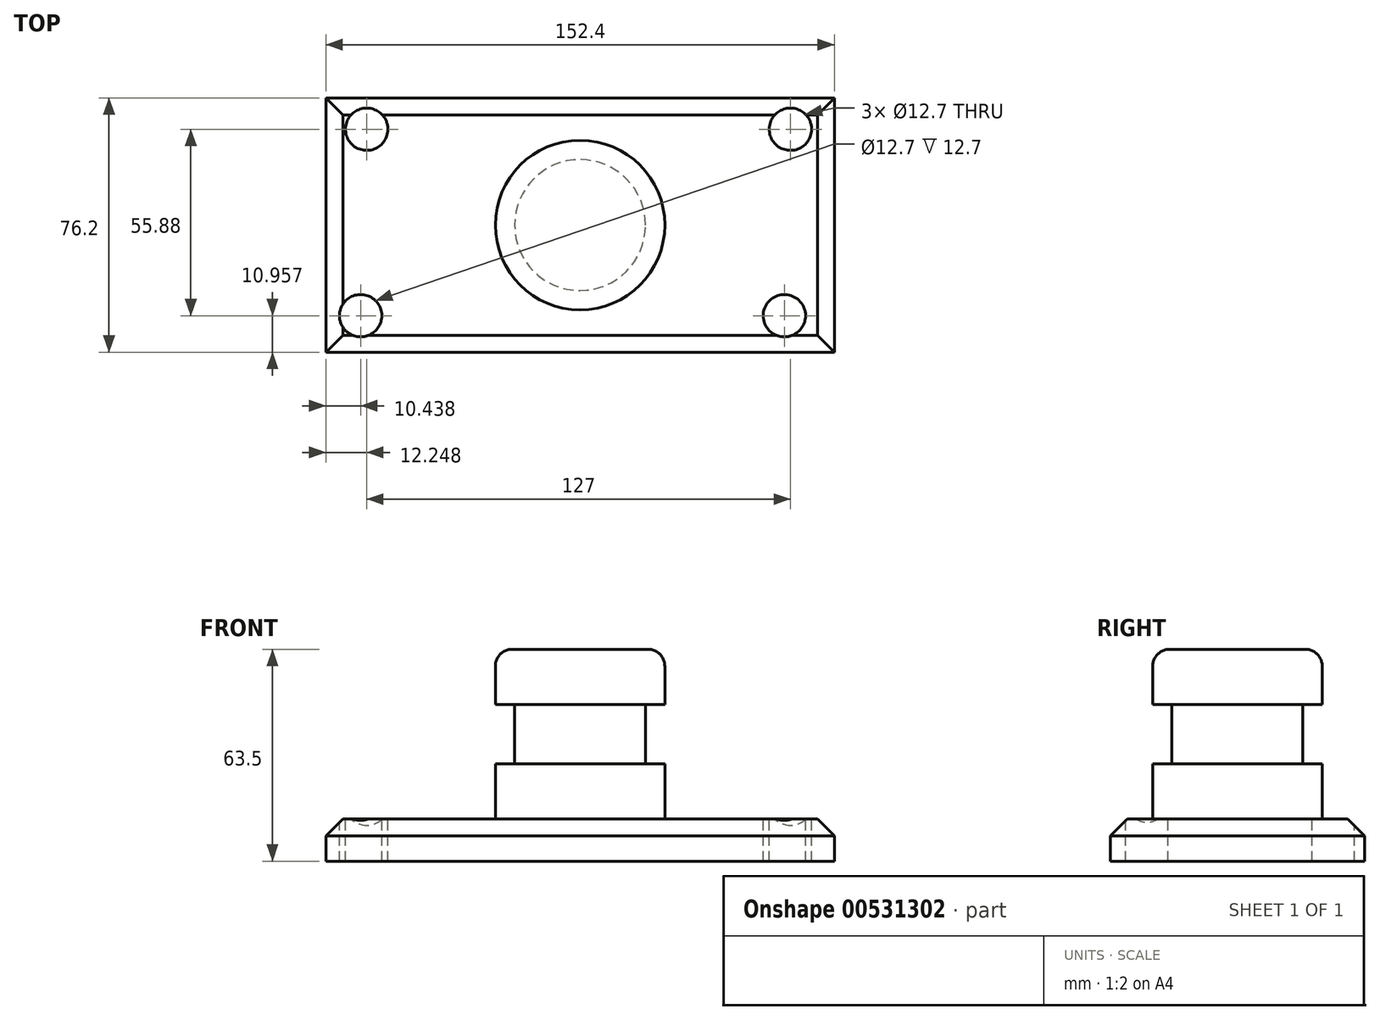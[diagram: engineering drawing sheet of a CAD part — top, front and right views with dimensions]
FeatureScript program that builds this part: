
annotation { "Feature Type Name" : "Feature", "Feature Type Description" : "" }
export const myFeature = defineFeature(function(context is Context, id is Id, definition is map)
    precondition{}
    {
        {
            var Q0;
            Q0=qCreatedBy(makeId("Top.planeOp"),FACE);
            var sketch = newSketch(context, id + "F0", { "sketchPlane" : qUnion([Q0])});
            skLineSegment(sketch, "E0.bottom", {"start": v(76.2, -38.1) * mm, "end": v(-76.2, -38.1) * mm});
            skLineSegment(sketch, "E0.top", {"start": v(76.2, 38.1) * mm, "end": v(-76.2, 38.1) * mm});
            skLineSegment(sketch, "E0.left", {"start": v(76.2, -38.1) * mm, "end": v(76.2, 38.1) * mm});
            skLineSegment(sketch, "E0.right", {"start": v(-76.2, -38.1) * mm, "end": v(-76.2, 38.1) * mm});
            skPoint(sketch, "E0.middle", {"position": v(0, 0) * mm});
            skSolve(sketch);
        }
        {
            var Q0;
            Q0 = qSketchRegion(id + "F0", true);
            extrude(context, id + "F1", {"entities" : qUnion([Q0]), "depth" : 12.7 * mm, "offsetDistance" : 25.4 * mm});
        }
        {
            var Q0;
            Q0=makeQuery(id+"F1.opExtrude","CAP_FACE",FACE,{"disambiguationData":[OSD([sQuery(id+"F0.wireOp",EDGE,"E0.bottom"),sQuery(id+"F0.wireOp",EDGE,"E0.top"),sQuery(id+"F0.wireOp",EDGE,"E0.left"),sQuery(id+"F0.wireOp",EDGE,"E0.right")])],"isStart":false});
            var sketch = newSketch(context, id + "F2", { "sketchPlane" : qUnion([Q0])});
            skCircle(sketch, "E1", {"center": v(-63.95, 28.74) * mm, "radius": 6.35 * mm});
            skCircle(sketch, "E2", {"center": v(-65.76, -27.14) * mm, "radius": 6.35 * mm});
            skCircle(sketch, "E3", {"center": v(61.24, -27.14) * mm, "radius": 6.35 * mm});
            skCircle(sketch, "E4", {"center": v(63.05, 28.74) * mm, "radius": 6.35 * mm});
            skSolve(sketch);
        }
        {
            var Q0;
            Q0=makeQuery(id+"F2.imprint","IMPRINT",FACE,{"disambiguationData":[TD([[makeQuery(id+"F2.imprint","IMPRINT",EDGE,{"derivedFrom":sQuery(id+"F2.wireOp",EDGE,"E1")}),1.0]])]});
            var Q1;
            Q1=makeQuery(id+"F2.imprint","IMPRINT",FACE,{"disambiguationData":[TD([[makeQuery(id+"F2.imprint","IMPRINT",EDGE,{"derivedFrom":sQuery(id+"F2.wireOp",EDGE,"E2")}),1.0]])]});
            var Q2;
            Q2=makeQuery(id+"F2.imprint","IMPRINT",FACE,{"disambiguationData":[TD([[makeQuery(id+"F2.imprint","IMPRINT",EDGE,{"derivedFrom":sQuery(id+"F2.wireOp",EDGE,"E4")}),1.0]])]});
            var Q3;
            Q3=makeQuery(id+"F2.imprint","IMPRINT",FACE,{"disambiguationData":[TD([[makeQuery(id+"F2.imprint","IMPRINT",EDGE,{"derivedFrom":sQuery(id+"F2.wireOp",EDGE,"E3")}),1.0]])]});
            extrude(context, id + "F3", {"entities" : qUnion([Q0, Q1, Q2, Q3]), "operationType" : NewBodyOperationType.REMOVE, "endBound" : BoundingType.THROUGH_ALL, "oppositeDirection" : true, "depth" : 12.7 * mm, "offsetDistance" : 25.4 * mm});
        }
        {
            var Q0;
            Q0=qCreatedBy(makeId("Front.planeOp"),FACE);
            var sketch = newSketch(context, id + "F4", { "sketchPlane" : qUnion([Q0])});
            skLineSegment(sketch, "E5.bottom", {"start": v(0, 12.7) * mm, "end": v(25.4, 12.7) * mm});
            skLineSegment(sketch, "E5.top", {"start": v(0, 63.5) * mm, "end": v(25.4, 63.5) * mm});
            skLineSegment(sketch, "E5.left", {"start": v(0, 12.7) * mm, "end": v(0, 63.5) * mm});
            skLineSegment(sketch, "E5.right", {"start": v(25.4, 12.7) * mm, "end": v(25.4, 63.5) * mm});
            skSolve(sketch);
        }
        {
            var Q0;
            Q0=makeQuery(id+"F4.imprint","IMPRINT",FACE,{"disambiguationData":[TD([[makeQuery(id+"F4.imprint","IMPRINT",EDGE,{"derivedFrom":sQuery(id+"F4.wireOp",EDGE,"E5.bottom")}),1.0]])]});
            var Q1;
            Q1=sQuery(id+"F4.wireOp",EDGE,"E5.left");
            revolve(context, id + "F5", {"operationType" : NewBodyOperationType.ADD, "entities" : qUnion([Q0]), "axis" : qUnion([Q1]), "revolveType" : RevolveType.FULL});
        }
        {
            var Q0;
            Q0=qCreatedBy(makeId("Front.planeOp"),FACE);
            var sketch = newSketch(context, id + "F6", { "sketchPlane" : qUnion([Q0])});
            skLineSegment(sketch, "E6.bottom", {"start": v(19.62, 46.99) * mm, "end": v(30.98, 46.99) * mm});
            skLineSegment(sketch, "E6.top", {"start": v(19.62, 29.2) * mm, "end": v(30.98, 29.2) * mm});
            skLineSegment(sketch, "E6.left", {"start": v(19.62, 46.99) * mm, "end": v(19.62, 29.2) * mm});
            skLineSegment(sketch, "E6.right", {"start": v(30.98, 46.99) * mm, "end": v(30.98, 29.2) * mm});
            skSolve(sketch);
        }
        {
            var Q0;
            Q0=makeQuery(id+"F6.imprint","IMPRINT",FACE,{"disambiguationData":[TD([[makeQuery(id+"F6.imprint","IMPRINT",EDGE,{"derivedFrom":sQuery(id+"F6.wireOp",EDGE,"E6.bottom")}),-1.0]])]});
            var Q1;
            Q1=makeQuery(id+"F5.opRevolve","SWEPT_FACE",FACE,{"disambiguationData":[OSD([sQuery(id+"F4.wireOp",EDGE,"E5.right")])]});
            revolve(context, id + "F7", {"operationType" : NewBodyOperationType.REMOVE, "entities" : qUnion([Q0]), "axis" : qUnion([Q1]), "revolveType" : RevolveType.FULL, "oppositeDirection" : true});
        }
        {
            var Q0;
            Q0=makeQuery(id+"F5.opRevolve","SWEPT_EDGE",EDGE,{"disambiguationData":[OSD([sQuery(id+"F4.wireOp",EDGE,"E5.top"),sQuery(id+"F4.wireOp",EDGE,"E5.right")])]});
            var Q1;
            Q1=makeQuery(id+"F5.opRevolve","SWEPT_EDGE",EDGE,{"disambiguationData":[OSD([sQuery(id+"F4.wireOp",EDGE,"E5.bottom"),sQuery(id+"F4.wireOp",EDGE,"E5.right")])]});
            fillet(context, id + "F8", {"entities" : qUnion([Q0, Q1]), "radius" : 5.08 * mm, "tangentPropagation" : true, "allowEdgeOverflow" : false});
        }
        {
            var Q0;
            Q0=makeQuery(id+"F1.opExtrude","CAP_EDGE",EDGE,{"disambiguationData":[OSD([sQuery(id+"F0.wireOp",EDGE,"E0.left")])],"isStart":false});
            var Q1;
            Q1=makeQuery(id+"F1.opExtrude","CAP_EDGE",EDGE,{"disambiguationData":[OSD([sQuery(id+"F0.wireOp",EDGE,"E0.top")])],"isStart":false});
            var Q2;
            Q2=makeQuery(id+"F1.opExtrude","CAP_EDGE",EDGE,{"disambiguationData":[OSD([sQuery(id+"F0.wireOp",EDGE,"E0.bottom")])],"isStart":false});
            var Q3;
            Q3=makeQuery(id+"F1.opExtrude","CAP_EDGE",EDGE,{"disambiguationData":[OSD([sQuery(id+"F0.wireOp",EDGE,"E0.right")])],"isStart":false});
            chamfer(context, id + "F9", {"entities" : qUnion([Q0, Q1, Q2, Q3]), "width" : 5.08 * mm, "tangentPropagation" : true});
        }
    });
